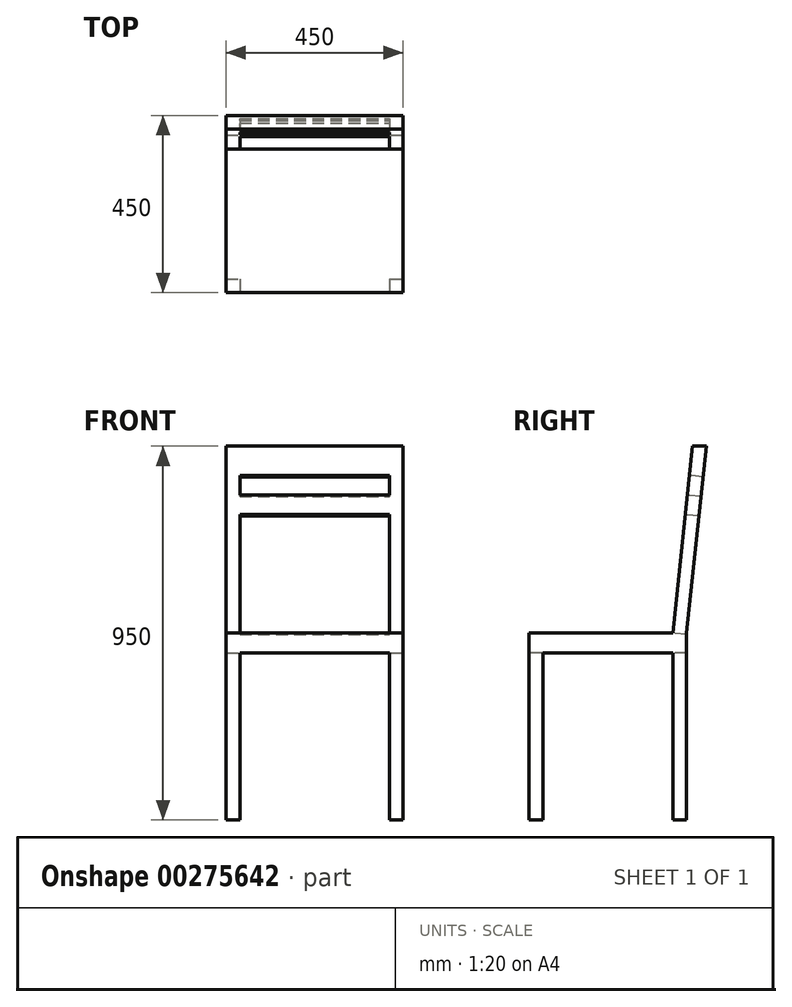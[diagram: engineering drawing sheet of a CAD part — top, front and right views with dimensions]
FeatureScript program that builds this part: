
annotation { "Feature Type Name" : "Feature", "Feature Type Description" : "" }
export const myFeature = defineFeature(function(context is Context, id is Id, definition is map)
    precondition{}
    {
        {
            var Q0;
            Q0=qCreatedBy(makeId("Top.planeOp"),FACE);
            var sketch = newSketch(context, id + "F0", { "sketchPlane" : qUnion([Q0])});
            skLineSegment(sketch, "E0.bottom", {"start": v(225, 225) * mm, "end": v(-225, 225) * mm});
            skLineSegment(sketch, "E0.top", {"start": v(225, -225) * mm, "end": v(-225, -225) * mm});
            skLineSegment(sketch, "E0.left", {"start": v(225, 225) * mm, "end": v(225, -225) * mm});
            skLineSegment(sketch, "E0.right", {"start": v(-225, 225) * mm, "end": v(-225, -225) * mm});
            skPoint(sketch, "E0.middle", {"position": v(0, 0) * mm});
            skSolve(sketch);
        }
        {
            var Q0;
            Q0=qSketchRegion(id+"F0",true);
            extrude(context, id + "F1", {"entities" : qUnion([Q0]), "depth" : 950 * mm});
        }
        {
            var Q0;
            Q0=makeQuery(id+"F1.opExtrude","SWEPT_FACE",FACE,{"disambiguationData":[OSD([sQuery(id+"F0.wireOp",EDGE,"E0.left")])]});
            var sketch = newSketch(context, id + "F2", { "sketchPlane" : qUnion([Q0])});
            skLineSegment(sketch, "E1.bottom", {"start": v(225, 475) * mm, "end": v(-225, 475) * mm});
            skLineSegment(sketch, "E1.top", {"start": v(225, 425) * mm, "end": v(-225, 425) * mm});
            skLineSegment(sketch, "E1.left", {"start": v(225, 475) * mm, "end": v(225, 425) * mm});
            skLineSegment(sketch, "E1.right", {"start": v(-225, 475) * mm, "end": v(-225, 425) * mm});
            skLineSegment(sketch, "E2", {"start": v(225, 950) * mm, "end": v(175, 475) * mm});
            skLineSegment(sketch, "E3", {"start": v(190, 950) * mm, "end": v(140, 475) * mm});
            skLineSegment(sketch, "E4", {"start": v(175, 475) * mm, "end": v(175, 0) * mm});
            skLineSegment(sketch, "E5", {"start": v(140, 475) * mm, "end": v(140, 0) * mm});
            skLineSegment(sketch, "E6.bottom", {"start": v(-225, 425) * mm, "end": v(-190, 425) * mm});
            skLineSegment(sketch, "E6.top", {"start": v(-225, 0) * mm, "end": v(-190, 0) * mm});
            skLineSegment(sketch, "E6.left", {"start": v(-225, 425) * mm, "end": v(-225, 0) * mm});
            skLineSegment(sketch, "E6.right", {"start": v(-190, 425) * mm, "end": v(-190, 0) * mm});
            skSolve(sketch);
        }
        {
            var Q0;
            {var subQ4=sQuery(id+"F2.wireOp",EDGE,"E3");Q0=makeQuery(id+"F2.imprint","IMPRINT",FACE,{"disambiguationData":[TD([[makeQuery(id+"F2.imprint","IMPRINT",EDGE,{"derivedFrom":subQ4}),-1.0]])]});}
            var Q1;
            {var subQ0=sQuery(id+"F2.wireOp",EDGE,"E6.right");Q1=makeQuery(id+"F2.imprint","IMPRINT",FACE,{"disambiguationData":[TD([[makeQuery(id+"F2.imprint","IMPRINT",EDGE,{"derivedFrom":subQ0}),1.0]])]});}
            var Q2;
            {var subQ1=sQuery(id+"F0.wireOp",EDGE,"E0.left");var subQ4=sQuery(id+"F2.wireOp",EDGE,"E4");var subQ6=makeQuery(id+"F1.opExtrude","CAP_EDGE",EDGE,{"disambiguationData":[OSD([subQ1])],"isStart":true});var subQ7=makeQuery(id+"F2.imprint","INTERSECT",VERTEX,{"derivedFrom":[subQ6,subQ4]});Q2=makeQuery(id+"F2.imprint","IMPRINT",FACE,{"disambiguationData":[TD([[makeQuery(id+"F2.imprint","IMPRINT",EDGE,{"disambiguationData":[TD([[subQ7,1.0]])],"derivedFrom":subQ4}),1.0]])]});}
            var Q3;
            {var subQ0=sQuery(id+"F2.wireOp",EDGE,"E1.left");Q3=makeQuery(id+"F2.imprint","IMPRINT",FACE,{"disambiguationData":[TD([[makeQuery(id+"F2.imprint","IMPRINT",EDGE,{"derivedFrom":subQ0}),-1.0]])]});}
            var Q4;
            {var subQ4=sQuery(id+"F2.wireOp",EDGE,"E2");Q4=makeQuery(id+"F2.imprint","IMPRINT",FACE,{"disambiguationData":[TD([[makeQuery(id+"F2.imprint","IMPRINT",EDGE,{"derivedFrom":subQ4}),1.0]])]});}
            extrude(context, id + "F3", {"entities" : qUnion([Q0, Q1, Q2, Q3, Q4]), "operationType" : NewBodyOperationType.REMOVE, "endBound" : BoundingType.THROUGH_ALL, "oppositeDirection" : true, "depth" : 25 * mm});
        }
        {
            var Q0;
            Q0=makeQuery(id+"F1.opExtrude","SWEPT_FACE",FACE,{"disambiguationData":[OSD([sQuery(id+"F0.wireOp",EDGE,"E0.top")])]});
            var sketch = newSketch(context, id + "F4", { "sketchPlane" : qUnion([Q0])});
            skLineSegment(sketch, "E7", {"start": v(-190, 0) * mm, "end": v(-190, 425) * mm});
            skLineSegment(sketch, "E8", {"start": v(-190, 425) * mm, "end": v(190, 425) * mm});
            skLineSegment(sketch, "E9", {"start": v(190, 425) * mm, "end": v(190, 0) * mm});
            skSolve(sketch);
        }
        {
            var Q0;
            {var subQ0=sQuery(id+"F4.wireOp",EDGE,"E7");Q0=makeQuery(id+"F4.imprint","IMPRINT",FACE,{"disambiguationData":[TD([[makeQuery(id+"F4.imprint","IMPRINT",EDGE,{"derivedFrom":subQ0}),-1.0]])]});}
            extrude(context, id + "F5", {"entities" : qUnion([Q0]), "operationType" : NewBodyOperationType.REMOVE, "endBound" : BoundingType.THROUGH_ALL, "oppositeDirection" : true, "depth" : 25 * mm});
        }
        {
            var Q0;
            Q0=makeQuery(id+"F3.boolean.opBoolean","COPY",FACE,{"derivedFrom":makeQuery(id+"F3.opExtrude","SWEPT_FACE",FACE,{"disambiguationData":[OSD([sQuery(id+"F2.wireOp",EDGE,"E3")])]})});
            var sketch = newSketch(context, id + "F6", { "sketchPlane" : qUnion([Q0])});
            skLineSegment(sketch, "E10", {"start": v(-190, 487.05) * mm, "end": v(-190, 889.67) * mm});
            skLineSegment(sketch, "E11", {"start": v(-190, 889.67) * mm, "end": v(190, 889.67) * mm});
            skLineSegment(sketch, "E12", {"start": v(190, 889.67) * mm, "end": v(190, 487.05) * mm});
            skLineSegment(sketch, "E13", {"start": v(-190, 839.67) * mm, "end": v(190, 839.67) * mm});
            skLineSegment(sketch, "E14", {"start": v(-190, 789.67) * mm, "end": v(190, 789.67) * mm});
            skSolve(sketch);
        }
        {
            var Q0;
            {var subQ3=sQuery(id+"F6.wireOp",EDGE,"E14");Q0=makeQuery(id+"F6.imprint","IMPRINT",FACE,{"disambiguationData":[TD([[makeQuery(id+"F6.imprint","IMPRINT",EDGE,{"derivedFrom":subQ3}),-1.0]])]});}
            var Q1;
            {var subQ0=sQuery(id+"F6.wireOp",EDGE,"E11");Q1=makeQuery(id+"F6.imprint","IMPRINT",FACE,{"disambiguationData":[TD([[makeQuery(id+"F6.imprint","IMPRINT",EDGE,{"derivedFrom":subQ0}),-1.0]])]});}
            extrude(context, id + "F7", {"entities" : qUnion([Q0, Q1]), "operationType" : NewBodyOperationType.REMOVE, "endBound" : BoundingType.THROUGH_ALL, "oppositeDirection" : true, "depth" : 25 * mm});
        }
    });
